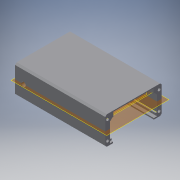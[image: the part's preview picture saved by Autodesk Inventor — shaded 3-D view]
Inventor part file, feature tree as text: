
AUTODESK INVENTOR PART (.ipt)
format: ipt  version: 2019.4 (Build 234330000, 330)  size: 493,056 bytes
history: native  units: mm
features: reference x12, extrude x11, other x11, plane x10, sketch x10, projected_geometry x9, chamfer x4, mirror x1
ambient origin geometry x8: Origin, YZ Plane, XZ Plane, XY Plane, X Axis, Y Axis, Z Axis, Center Point
bodies: Volumenkörper2 (feature_tree)
feature tree (68):
  plane  "Arbeitsebene6"
  sketch  "Skizze6"  dims[d39=1.0mm d42=0.1mm]
  plane  "Arbeitsebene7"
  extrude  "Extrusion6"  Depth=0.1mm
  extrude  "Extrusion7"  Depth=2.0mm
  plane  "Arbeitsebene8"
  extrude  "Extrusion8"  Depth=3.9mm
  chamfer  "Fase1"  Distance=2.0mm
  chamfer  "Fase2"  Distance=50.0mm
  extrude  "Extrusion10"  Depth=2.0mm TaperAngle=45.0deg
  sketch  "Skizze12"  dims[d54=8.9mm d56=2.0mm d57=0.0mm]
  plane  "Arbeitsebene9"
  extrude  "Extrusion11"  Depth=10.0mm TaperAngle=0.0deg
  extrude  "Extrusion12"  Depth=8.0mm TaperAngle=0.0deg
  chamfer  "Fase4"  Distance=2.0mm Angle=45.0deg
  plane  "Arbeitsebene10"
  chamfer  "Fase5"  Distance=0.75mm
  other  "Arbeitspunkt3"
  plane  "Arbeitsebene11"
  extrude  "Extrusion17"  Depth=2.0mm
  mirror  "Spiegeln2"
  extrude  "Extrusion21"  Depth=2.0mm TaperAngle=45.0deg
  extrude  "Extrusion22"  Depth=2.0mm
  extrude  "Extrusion23"  Depth=2.0mm
  extrude  "Extrusion24"  Depth=10.0mm TaperAngle=0.0deg
  reference  "Referenz13"
  reference  "Referenz14"
  reference  "Referenz15"
  reference  "Referenz16"
  reference  "Referenz17"
  reference  "Referenz18"
  reference  "Referenz19"
  reference  "Referenz20"
  reference  "Referenz21"
  reference  "Referenz22"
  reference  "Referenz23"
  projected_geometry  "Projizierte Kontur5"
  sketch  "Skizze8"  dims[d43=2.0mm d44=0.0mm d48=4.3mm]
  sketch  "Skizze11"  dims[d51=17.4mm d52=17.9mm d53=3.9mm]
  projected_geometry  "Projizierte Kontur8"
  sketch  "Skizze13"  dims[d58=8.9mm d72=50.0mm d73=0.0mm]
  other  "Arbeitsachse1"
  sketch  "Skizze18"  dims[d87=1.0mm d88=2.0mm d89=45.0deg d90=1.0mm d91=2.0mm d92=45.0deg]
  projected_geometry  "Projizierte Kontur14"
  projected_geometry  "Projizierte Kontur18"
  plane  "Arbeitsebene16"
  plane  "Arbeitsebene17"
  plane  "Arbeitsebene18"
  plane  "Arbeitsebene19"
  other  "Arbeitspunkt4"
  sketch  "Skizze22"  dims[d93=2.8mm d94=10.0mm d95=0.0mm]
  projected_geometry  "Projizierte Kontur19"
  sketch  "Skizze23"  dims[d96=13.0mm d97=0.0mm d103=8.0mm d104=0.0mm]
  projected_geometry  "Projizierte Kontur20"
  reference  "Referenz48"
  sketch  "Skizze24"  dims[d113=36.0mm d126=3.0mm d127=2.0mm d128=45.0deg]
  projected_geometry  "Projizierte Kontur21"
  projected_geometry  "Projizierte Kontur22"
  sketch  "Sketch25"  dims[d132=0.0mm d135=0.75mm d136=0.65mm d137=1.0mm d138=2.0mm d139=45.0deg d141=8.4mm d142=0.2mm d143=10.0mm d144=0.0mm d157=2.5mm d160=17.9mm d161=8.9mm d162=1.7mm d163=3.5mm d164=3.5mm d166=3.5mm d167=0.75mm d168=2.5mm d169=2.8mm d170=1.0mm d171=0.0mm d172=2.0mm d175=2.0mm d178=1.0mm d179=0.0mm d180=1.0mm d181=0.0mm d182=3.0mm d183=3.0mm d184=0.0mm d185=0.0mm d186=1.0mm d187=1.0mm d188=1.0mm d189=1.0mm d190=1.9mm d191=1.9mm d192=2.0mm d193=0.0mm]
  projected_geometry  "Projected Loop23"
  other  "<userpath>\Documents\Inventor\HITscope\HITscope_v0.iam"
  other  "HITscope_v0.iam"
  other  "00_ESP32_Board:1"
  other  "Assembly_Omniscope_v1.iam"
  other  "01_Camera_Module_Lit:1"
  other  "<userpath>\Documents\Inventor\HITscope\Assembly_HITscope.iam"
  other  "Assembly_HITscope.iam"
  other  "HITscope_v0:1"
